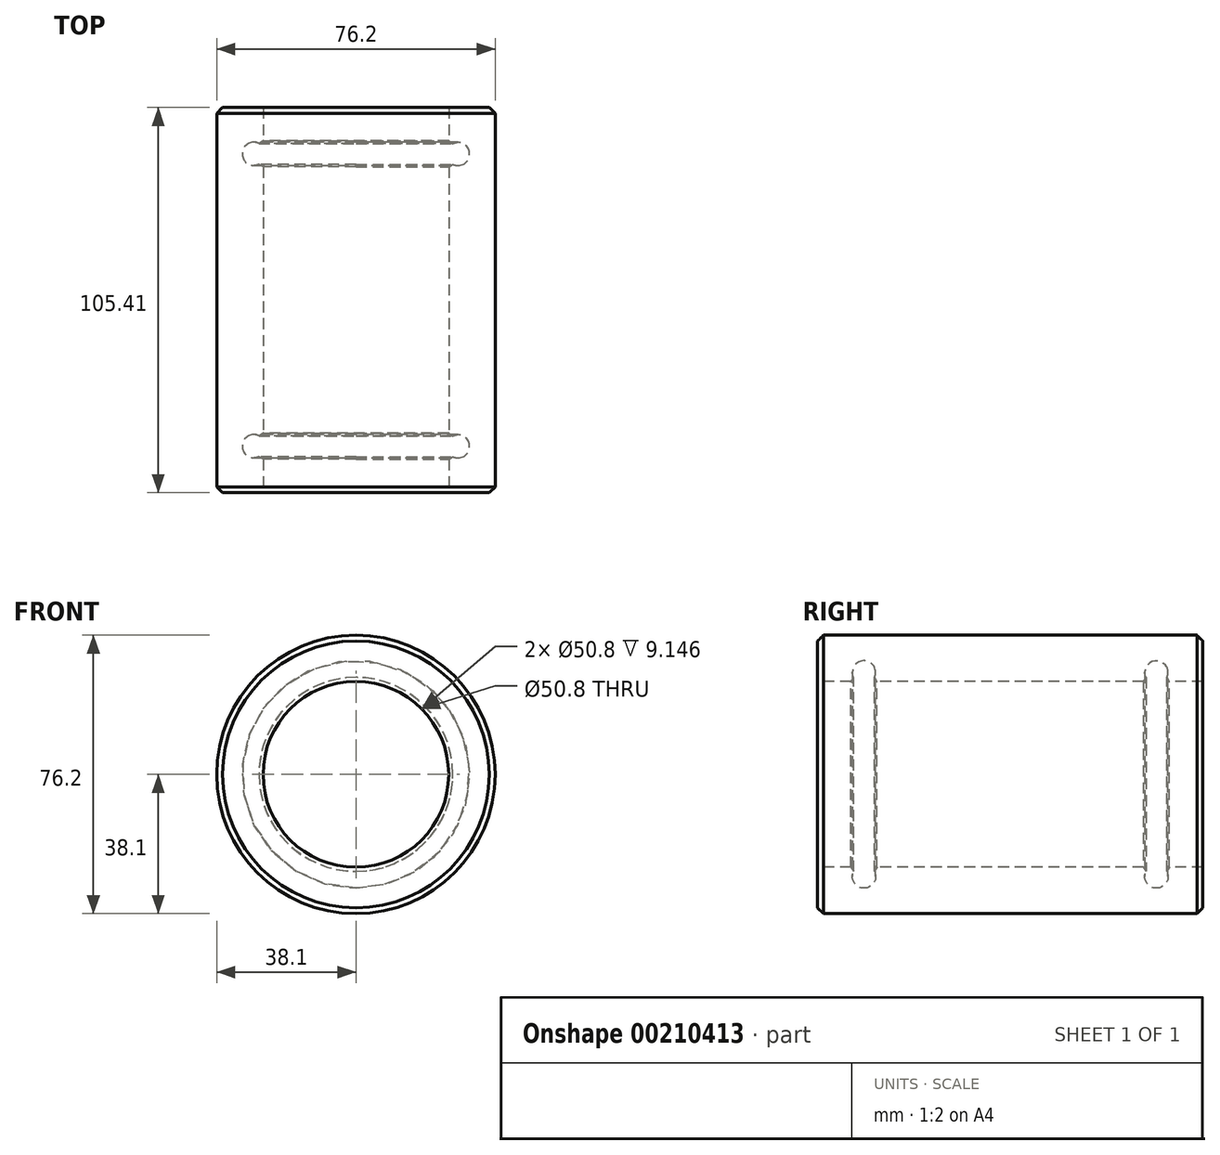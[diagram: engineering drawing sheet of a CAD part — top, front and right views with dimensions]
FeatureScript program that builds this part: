
annotation { "Feature Type Name" : "Feature", "Feature Type Description" : "" }
export const myFeature = defineFeature(function(context is Context, id is Id, definition is map)
    precondition{}
    {
        {
            var Q0;
            Q0=qCreatedBy(makeId("Right.planeOp"),FACE);
            var sketch = newSketch(context, id + "F0", { "sketchPlane" : qUnion([Q0])});
            skLineSegment(sketch, "E0", {"start": v(0, 0) * mm, "end": v(127, 0) * mm, "construction": true});
            skLineSegment(sketch, "E1.bottom", {"start": v(0, 38.1) * mm, "end": v(105.41, 38.1) * mm});
            skLineSegment(sketch, "E1.top", {"start": v(0, 25.4) * mm, "end": v(10.8, 25.4) * mm});
            skLineSegment(sketch, "E1.left", {"start": v(0, 38.1) * mm, "end": v(0, 25.4) * mm});
            skLineSegment(sketch, "E1.right", {"start": v(105.41, 38.1) * mm, "end": v(105.41, 25.4) * mm});
            skArc(sketch, "E2", {"start": v(94.61, 25.4) * mm, "mid": v(92.71, 31.12) * mm, "end": v(90.8, 25.4) * mm});
            skLineSegment(sketch, "E3.trimOffspring", {"start": v(14.6, 25.4) * mm, "end": v(90.8, 25.4) * mm});
            skArc(sketch, "E4", {"start": v(14.6, 25.4) * mm, "mid": v(12.7, 31.12) * mm, "end": v(10.8, 25.4) * mm});
            skLineSegment(sketch, "E5.trimOffspring", {"start": v(94.61, 25.4) * mm, "end": v(105.41, 25.4) * mm});
            skSolve(sketch);
        }
        {
            var Q0;
            Q0=makeQuery(id+"F0.imprint","IMPRINT",FACE,{"disambiguationData":[TD([[makeQuery(id+"F0.imprint","IMPRINT",EDGE,{"derivedFrom":sQuery(id+"F0.wireOp",EDGE,"E1.bottom")}),-1.0]])]});
            var Q1;
            Q1=sQuery(id+"F0.wireOp",EDGE,"E0");
            revolve(context, id + "F1", {"entities" : qUnion([Q0]), "axis" : qUnion([Q1]), "revolveType" : RevolveType.FULL});
        }
        {
            var Q0;
            Q0=makeQuery(id+"F1.opRevolve","SWEPT_FACE",FACE,{"disambiguationData":[OSD([sQuery(id+"F0.wireOp",EDGE,"E4")])]});
            var Q1;
            Q1=makeQuery(id+"F1.opRevolve","SWEPT_FACE",FACE,{"disambiguationData":[OSD([sQuery(id+"F0.wireOp",EDGE,"E2")])]});
            chamfer(context, id + "F2", {"entities" : qUnion([Q0, Q1]), "width" : 0.79 * mm, "tangentPropagation" : true});
        }
        {
            var Q0;
            Q0=makeQuery(id+"F1.opRevolve","SWEPT_EDGE",EDGE,{"disambiguationData":[OSD([sQuery(id+"F0.wireOp",EDGE,"E1.bottom"),sQuery(id+"F0.wireOp",EDGE,"E1.right")])]});
            var Q1;
            Q1=makeQuery(id+"F1.opRevolve","SWEPT_EDGE",EDGE,{"disambiguationData":[OSD([sQuery(id+"F0.wireOp",EDGE,"E1.bottom"),sQuery(id+"F0.wireOp",EDGE,"E1.left")])]});
            chamfer(context, id + "F3", {"entities" : qUnion([Q0, Q1]), "width" : 1.6 * mm, "tangentPropagation" : true});
        }
    });
